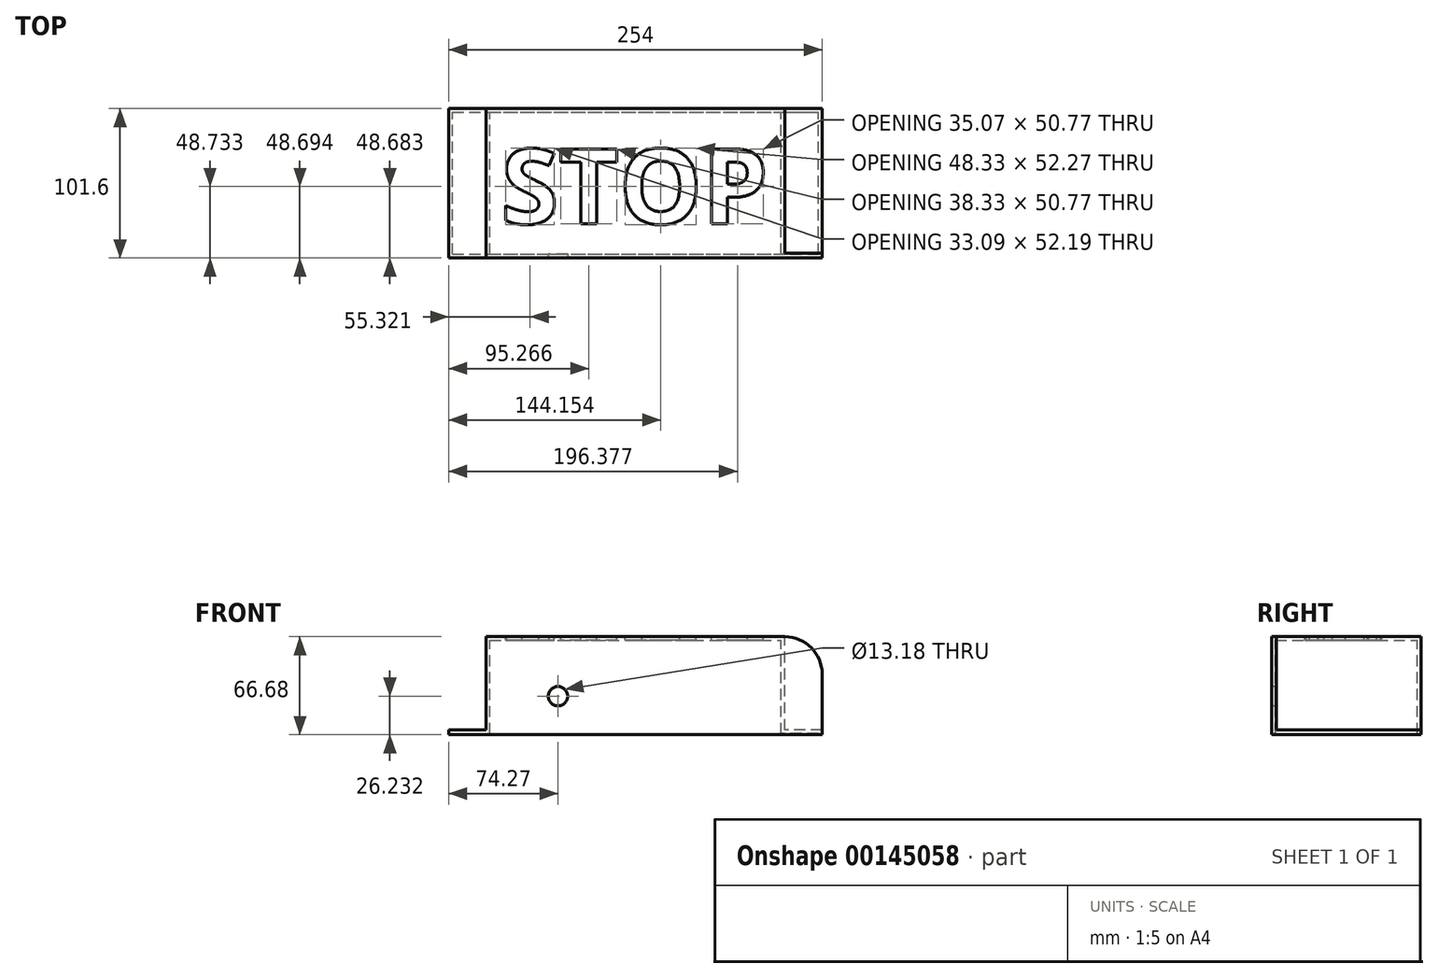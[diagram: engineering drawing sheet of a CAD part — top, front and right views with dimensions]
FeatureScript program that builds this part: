
annotation { "Feature Type Name" : "Feature", "Feature Type Description" : "" }
export const myFeature = defineFeature(function(context is Context, id is Id, definition is map)
    precondition{}
    {
        {
            var Q0;
            Q0=qCreatedBy(makeId("Front.planeOp"),FACE);
            var sketch = newSketch(context, id + "F0", { "sketchPlane" : qUnion([Q0])});
            skLineSegment(sketch, "E0.bottom", {"start": v(-127, 1.59) * mm, "end": v(127, 1.59) * mm});
            skLineSegment(sketch, "E0.top", {"start": v(-127, -1.59) * mm, "end": v(127, -1.59) * mm});
            skLineSegment(sketch, "E0.left", {"start": v(-127, 1.59) * mm, "end": v(-127, -1.59) * mm});
            skLineSegment(sketch, "E0.right", {"start": v(127, 1.59) * mm, "end": v(127, -1.59) * mm});
            skPoint(sketch, "E0.middle", {"position": v(0, 0) * mm});
            skLineSegment(sketch, "E1.bottom", {"start": v(-101.6, 1.59) * mm, "end": v(101.6, 1.59) * mm});
            skLineSegment(sketch, "E1.top", {"start": v(-101.6, 65.09) * mm, "end": v(101.6, 65.09) * mm});
            skLineSegment(sketch, "E1.left", {"start": v(-101.6, 1.59) * mm, "end": v(-101.6, 65.09) * mm});
            skLineSegment(sketch, "E1.right", {"start": v(101.6, 1.59) * mm, "end": v(101.6, 65.09) * mm});
            skSolve(sketch);
        }
        {
            var Q0;
            Q0 = qSketchRegion(id + "F0", true);
            extrude(context, id + "F1", {"entities" : qUnion([Q0]), "endBound" : BoundingType.SYMMETRIC, "depth" : 101.6 * mm});
        }
        {
            var Q0;
            Q0=makeQuery(id+"F1.opExtrude","SWEPT_FACE",FACE,{"disambiguationData":[OSD([sQuery(id+"F0.wireOp",EDGE,"E1.right")])]});
            var sketch = newSketch(context, id + "F2", { "sketchPlane" : qUnion([Q0])});
            skLineSegment(sketch, "E2.bottom", {"start": v(-50.8, 1.59) * mm, "end": v(-47.63, 1.59) * mm});
            skLineSegment(sketch, "E2.top", {"start": v(-50.8, 65.09) * mm, "end": v(-47.63, 65.09) * mm});
            skLineSegment(sketch, "E2.left", {"start": v(-50.8, 1.59) * mm, "end": v(-50.8, 65.09) * mm});
            skLineSegment(sketch, "E2.right", {"start": v(-47.63, 1.59) * mm, "end": v(-47.63, 65.09) * mm});
            skSolve(sketch);
        }
        {
            var Q0;
            Q0=makeQuery(id+"F2.imprint","IMPRINT",FACE,{"disambiguationData":[TD([[makeQuery(id+"F2.imprint","IMPRINT",EDGE,{"derivedFrom":sQuery(id+"F2.wireOp",EDGE,"E2.bottom")}),1.0]])]});
            extrude(context, id + "F3", {"entities" : qUnion([Q0]), "operationType" : NewBodyOperationType.ADD, "depth" : 25.4 * mm});
        }
        {
            var Q0;
            Q0=makeQuery(id+"F3.boolean.opBoolean","MERGE",FACE,{"derivedFrom":[makeQuery(id+"F1.opExtrude","SWEPT_FACE",FACE,{"disambiguationData":[OSD([sQuery(id+"F0.wireOp",EDGE,"E1.top")])]}),makeQuery(id+"F3.opExtrude","SWEPT_FACE",FACE,{"disambiguationData":[OSD([sQuery(id+"F2.wireOp",EDGE,"E2.top")])]})]});
            var sketch = newSketch(context, id + "F4", { "sketchPlane" : qUnion([Q0])});
            skText(sketch, "E3", { "text": "STOP\n", "fontName": "OpenSans-Bold.ttf"});
            const initialGuessF4  = {"E3": [-0.09149, -0.0275, 1, 0, 0.0512]};
            skSetInitialGuess(sketch, initialGuessF4);
            skSolve(sketch);
        }
        {
            var Q0;
            Q0=makeQuery(id+"F1.opExtrude","SWEPT_FACE",FACE,{"disambiguationData":[OSD([sQuery(id+"F0.wireOp",EDGE,"E0.top")])]});
            shell(context, id + "F5", {"entities" : qUnion([Q0]), "thickness" : 2.54 * mm});
        }
        {
            var Q0;
            Q0 = qSketchRegion(id + "F4", true);
            extrude(context, id + "F6", {"entities" : qUnion([Q0]), "operationType" : NewBodyOperationType.REMOVE, "oppositeDirection" : true, "depth" : 25.4 * mm});
        }
        {
            var Q0;
            Q0=makeQuery(id+"F3.opExtrude","CAP_EDGE",EDGE,{"disambiguationData":[OSD([sQuery(id+"F2.wireOp",EDGE,"E2.top")])],"isStart":false});
            fillet(context, id + "F7", {"entities" : qUnion([Q0]), "radius" : 25.4 * mm, "tangentPropagation" : true, "allowEdgeOverflow" : false});
        }
        {
            var Q0;
            Q0=makeQuery(id+"F3.boolean.opBoolean","MERGE",FACE,{"derivedFrom":[makeQuery(id+"F1.opExtrude","CAP_FACE",FACE,{"disambiguationData":[OSD([sQuery(id+"F0.wireOp",EDGE,"E0.bottom"),sQuery(id+"F0.wireOp",EDGE,"E0.top"),sQuery(id+"F0.wireOp",EDGE,"E0.left"),sQuery(id+"F0.wireOp",EDGE,"E0.right"),sQuery(id+"F0.wireOp",EDGE,"E1.top"),sQuery(id+"F0.wireOp",EDGE,"E1.left"),sQuery(id+"F0.wireOp",EDGE,"E1.right")])],"isStart":false}),makeQuery(id+"F3.opExtrude","SWEPT_FACE",FACE,{"disambiguationData":[OSD([sQuery(id+"F2.wireOp",EDGE,"E2.left")])]})]});
            var sketch = newSketch(context, id + "F8", { "sketchPlane" : qUnion([Q0])});
            skCircle(sketch, "E4", {"center": v(-52.73, 24.64) * mm, "radius": 6.59 * mm});
            skSolve(sketch);
        }
        {
            var Q0;
            Q0 = qSketchRegion(id + "F8", true);
            extrude(context, id + "F9", {"entities" : qUnion([Q0]), "operationType" : NewBodyOperationType.REMOVE, "oppositeDirection" : true, "depth" : 25.4 * mm});
        }
    });
